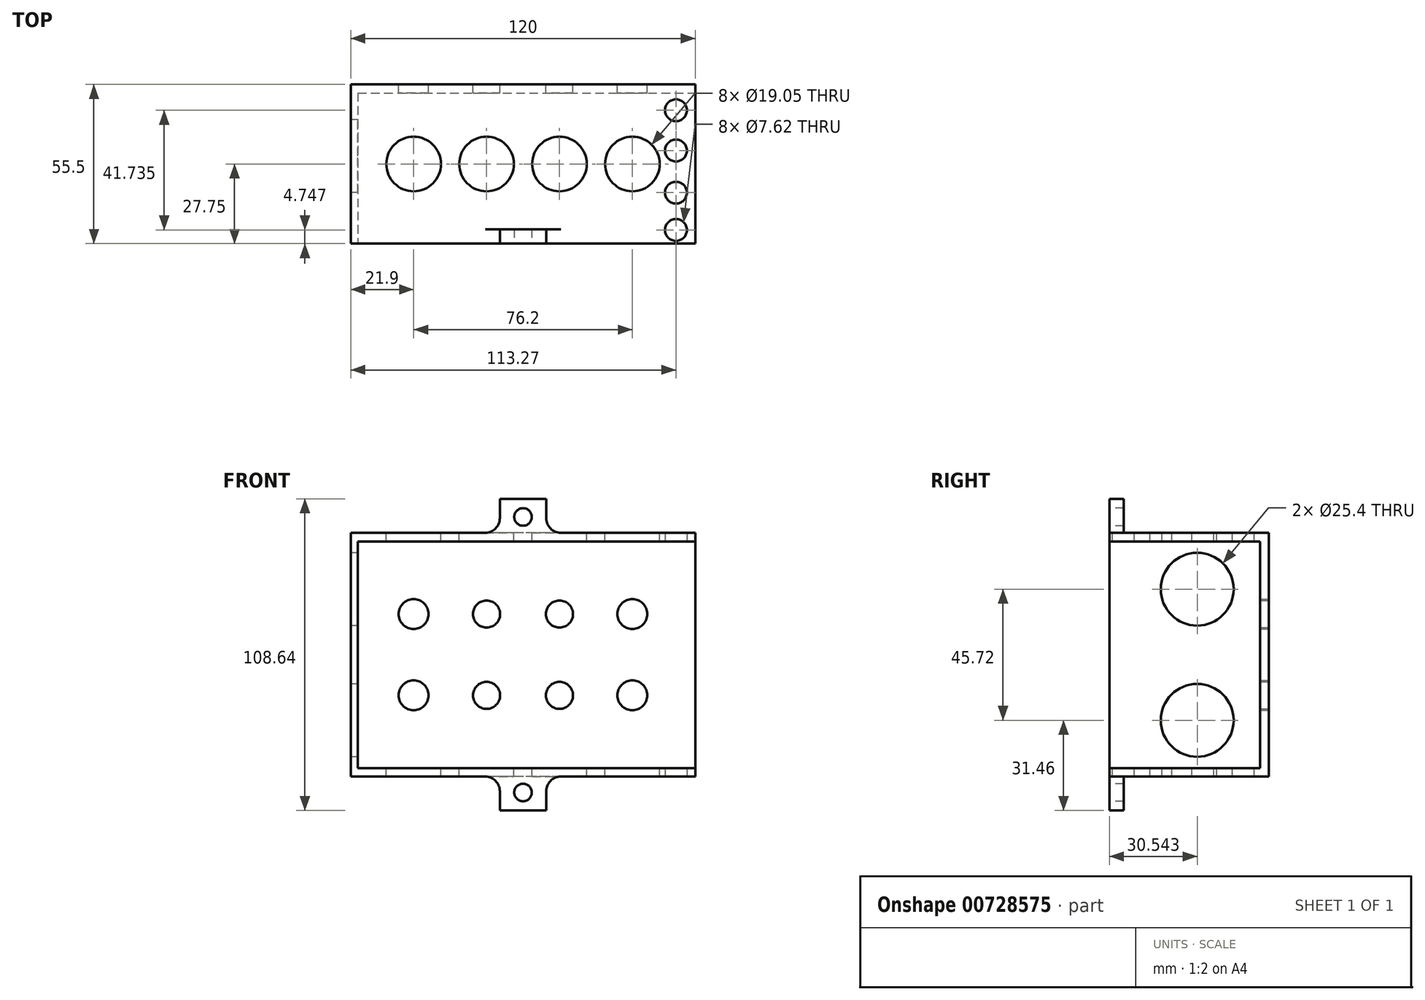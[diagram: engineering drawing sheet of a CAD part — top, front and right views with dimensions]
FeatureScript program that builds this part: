
annotation { "Feature Type Name" : "Feature", "Feature Type Description" : "" }
export const myFeature = defineFeature(function(context is Context, id is Id, definition is map)
    precondition{}
    {
        {
            var Q0;
            Q0=qCreatedBy(makeId("Front.planeOp"),FACE);
            var sketch = newSketch(context, id + "F0", { "sketchPlane" : qUnion([Q0])});
            skLineSegment(sketch, "E0.bottom", {"start": v(60, 42.5) * mm, "end": v(-60, 42.5) * mm});
            skLineSegment(sketch, "E0.top", {"start": v(60, -42.5) * mm, "end": v(-60, -42.5) * mm});
            skLineSegment(sketch, "E0.left", {"start": v(60, 42.5) * mm, "end": v(60, -42.5) * mm});
            skLineSegment(sketch, "E0.right", {"start": v(-60, 42.5) * mm, "end": v(-60, -42.5) * mm});
            skPoint(sketch, "E0.middle", {"position": v(0, 0) * mm});
            skCircle(sketch, "E1", {"center": v(-38.1, 14.17) * mm, "radius": 5.2 * mm});
            skCircle(sketch, "E2", {"center": v(-12.7, 14.17) * mm, "radius": 4.71 * mm});
            skCircle(sketch, "E3.MirrorC", {"center": v(12.7, 14.17) * mm, "radius": 4.71 * mm});
            skCircle(sketch, "E4.MirrorC", {"center": v(38.1, 14.17) * mm, "radius": 5.2 * mm});
            skCircle(sketch, "E5.MirrorC", {"center": v(-38.1, -14.17) * mm, "radius": 5.2 * mm});
            skCircle(sketch, "E6.MirrorC", {"center": v(-12.7, -14.17) * mm, "radius": 4.71 * mm});
            skCircle(sketch, "E7.MirrorC", {"center": v(12.7, -14.17) * mm, "radius": 4.71 * mm});
            skCircle(sketch, "E8.MirrorC", {"center": v(38.1, -14.17) * mm, "radius": 5.2 * mm});
            skSolve(sketch);
        }
        {
            var Q0;
            Q0 = qSketchRegion(id + "F0", true);
            extrude(context, id + "F1", {"entities" : qUnion([Q0]), "depth" : 3 * mm, "offsetDistance" : 25.4 * mm});
        }
        {
            var Q0;
            Q0=makeQuery(id+"F1.opExtrude","CAP_FACE",FACE,{"disambiguationData":[OSD([sQuery(id+"F0.wireOp",EDGE,"E0.bottom"),sQuery(id+"F0.wireOp",EDGE,"E0.top"),sQuery(id+"F0.wireOp",EDGE,"E0.left"),sQuery(id+"F0.wireOp",EDGE,"E0.right"),sQuery(id+"F0.wireOp",EDGE,"E1"),sQuery(id+"F0.wireOp",EDGE,"E2"),sQuery(id+"F0.wireOp",EDGE,"E3.MirrorC"),sQuery(id+"F0.wireOp",EDGE,"E4.MirrorC"),sQuery(id+"F0.wireOp",EDGE,"E5.MirrorC"),sQuery(id+"F0.wireOp",EDGE,"E6.MirrorC"),sQuery(id+"F0.wireOp",EDGE,"E7.MirrorC"),sQuery(id+"F0.wireOp",EDGE,"E8.MirrorC")])],"isStart":false});
            var sketch = newSketch(context, id + "F2", { "sketchPlane" : qUnion([Q0])});
            skLineSegment(sketch, "E9.bottom", {"start": v(-60, 42.5) * mm, "end": v(60, 42.5) * mm});
            skLineSegment(sketch, "E9.top", {"start": v(-60, 39.5) * mm, "end": v(60, 39.5) * mm});
            skLineSegment(sketch, "E9.left", {"start": v(-60, 42.5) * mm, "end": v(-60, 39.5) * mm});
            skLineSegment(sketch, "E9.right", {"start": v(60, 42.5) * mm, "end": v(60, 39.5) * mm});
            skLineSegment(sketch, "E10.MirrorCS", {"start": v(-60, -39.5) * mm, "end": v(60, -39.5) * mm});
            skLineSegment(sketch, "E11.MirrorCS", {"start": v(-60, -42.5) * mm, "end": v(60, -42.5) * mm});
            skSolve(sketch);
        }
        {
            var Q0;
            Q0 = qSketchRegion(id + "F2", true);
            extrude(context, id + "F3", {"entities" : qUnion([Q0]), "operationType" : NewBodyOperationType.ADD, "depth" : 52.5 * mm, "offsetDistance" : 25.4 * mm});
        }
        {
            var Q0;
            Q0=makeQuery(id+"F1.opExtrude","SWEPT_BODY",BODY,{"disambiguationData":[OSD([sQuery(id+"F0.wireOp",EDGE,"E0.bottom"),sQuery(id+"F0.wireOp",EDGE,"E0.top"),sQuery(id+"F0.wireOp",EDGE,"E0.left"),sQuery(id+"F0.wireOp",EDGE,"E0.right"),sQuery(id+"F0.wireOp",EDGE,"E1"),sQuery(id+"F0.wireOp",EDGE,"E2"),sQuery(id+"F0.wireOp",EDGE,"E3.MirrorC"),sQuery(id+"F0.wireOp",EDGE,"E4.MirrorC"),sQuery(id+"F0.wireOp",EDGE,"E5.MirrorC"),sQuery(id+"F0.wireOp",EDGE,"E6.MirrorC"),sQuery(id+"F0.wireOp",EDGE,"E7.MirrorC"),sQuery(id+"F0.wireOp",EDGE,"E8.MirrorC")])]});
            var Q1;
            Q1=qCreatedBy(makeId("Top.planeOp"),FACE);
            mirror(context, id + "F4", {"operationType" : NewBodyOperationType.ADD, "entities" : qUnion([Q0]), "mirrorPlane" : qUnion([Q1])});
        }
        {
            var Q0;
            Q0=makeQuery(id+"F3.opExtrude","CAP_FACE",FACE,{"disambiguationData":[OSD([sQuery(id+"F2.wireOp",EDGE,"E9.bottom"),sQuery(id+"F2.wireOp",EDGE,"E9.top"),sQuery(id+"F2.wireOp",EDGE,"E9.left"),sQuery(id+"F2.wireOp",EDGE,"E9.right")])],"isStart":false});
            var sketch = newSketch(context, id + "F5", { "sketchPlane" : qUnion([Q0])});
            skLineSegment(sketch, "E12.bottom", {"start": v(8.07, 54.32) * mm, "end": v(-8.07, 54.32) * mm});
            skLineSegment(sketch, "E12.top", {"start": v(8.07, 41.74) * mm, "end": v(-8.07, 41.74) * mm});
            skLineSegment(sketch, "E12.left", {"start": v(8.07, 54.32) * mm, "end": v(8.07, 41.74) * mm});
            skLineSegment(sketch, "E12.right", {"start": v(-8.07, 54.32) * mm, "end": v(-8.07, 41.74) * mm});
            skPoint(sketch, "E12.middle", {"position": v(0, 48.03) * mm});
            skCircle(sketch, "E13", {"center": v(0, 48.03) * mm, "radius": 3.06 * mm});
            skSolve(sketch);
        }
        {
            var Q0;
            Q0 = qSketchRegion(id + "F5", true);
            extrude(context, id + "F6", {"entities" : qUnion([Q0]), "operationType" : NewBodyOperationType.ADD, "oppositeDirection" : true, "depth" : 5 * mm, "offsetDistance" : 25.4 * mm});
        }
        {
            var Q0;
            Q0=makeQuery(id+"F6.boolean.opBoolean","INTERSECT",EDGE,{"derivedFrom":[makeQuery(id+"F3.boolean.opBoolean","MERGE",FACE,{"derivedFrom":[makeQuery(id+"F1.opExtrude","SWEPT_FACE",FACE,{"disambiguationData":[OSD([sQuery(id+"F0.wireOp",EDGE,"E0.bottom")])]}),makeQuery(id+"F3.opExtrude","SWEPT_FACE",FACE,{"disambiguationData":[OSD([sQuery(id+"F2.wireOp",EDGE,"E9.bottom")])]})]}),makeQuery(id+"F6.opExtrude","SWEPT_FACE",FACE,{"disambiguationData":[OSD([sQuery(id+"F5.wireOp",EDGE,"E12.right")])]})]});
            var Q1;
            Q1=makeQuery(id+"F6.boolean.opBoolean","INTERSECT",EDGE,{"derivedFrom":[makeQuery(id+"F3.boolean.opBoolean","MERGE",FACE,{"derivedFrom":[makeQuery(id+"F1.opExtrude","SWEPT_FACE",FACE,{"disambiguationData":[OSD([sQuery(id+"F0.wireOp",EDGE,"E0.bottom")])]}),makeQuery(id+"F3.opExtrude","SWEPT_FACE",FACE,{"disambiguationData":[OSD([sQuery(id+"F2.wireOp",EDGE,"E9.bottom")])]})]}),makeQuery(id+"F6.opExtrude","SWEPT_FACE",FACE,{"disambiguationData":[OSD([sQuery(id+"F5.wireOp",EDGE,"E12.left")])]})]});
            fillet(context, id + "F7", {"entities" : qUnion([Q0, Q1]), "radius" : 5.08 * mm, "tangentPropagation" : true, "allowEdgeOverflow" : false});
        }
        {
            var Q0;
            Q0=makeQuery(id+"F1.opExtrude","SWEPT_BODY",BODY,{"disambiguationData":[OSD([sQuery(id+"F0.wireOp",EDGE,"E0.bottom"),sQuery(id+"F0.wireOp",EDGE,"E0.top"),sQuery(id+"F0.wireOp",EDGE,"E0.left"),sQuery(id+"F0.wireOp",EDGE,"E0.right"),sQuery(id+"F0.wireOp",EDGE,"E1"),sQuery(id+"F0.wireOp",EDGE,"E2"),sQuery(id+"F0.wireOp",EDGE,"E3.MirrorC"),sQuery(id+"F0.wireOp",EDGE,"E4.MirrorC"),sQuery(id+"F0.wireOp",EDGE,"E5.MirrorC"),sQuery(id+"F0.wireOp",EDGE,"E6.MirrorC"),sQuery(id+"F0.wireOp",EDGE,"E7.MirrorC"),sQuery(id+"F0.wireOp",EDGE,"E8.MirrorC")])]});
            var Q1;
            Q1=qCreatedBy(makeId("Top.planeOp"),FACE);
            mirror(context, id + "F8", {"operationType" : NewBodyOperationType.ADD, "entities" : qUnion([Q0]), "mirrorPlane" : qUnion([Q1])});
        }
        {
            var Q0;
            Q0=makeQuery(id+"F3.boolean.opBoolean","MERGE",FACE,{"derivedFrom":[makeQuery(id+"F1.opExtrude","SWEPT_FACE",FACE,{"disambiguationData":[OSD([sQuery(id+"F0.wireOp",EDGE,"E0.bottom")])]}),makeQuery(id+"F3.opExtrude","SWEPT_FACE",FACE,{"disambiguationData":[OSD([sQuery(id+"F2.wireOp",EDGE,"E9.bottom")])]})]});
            var sketch = newSketch(context, id + "F9", { "sketchPlane" : qUnion([Q0])});
            skCircle(sketch, "E14", {"center": v(-38.1, -27.75) * mm, "radius": 9.53 * mm});
            skPoint(sketch, "E14.centerSnap0", {"position": v(-60, -27.75) * mm});
            skCircle(sketch, "E15", {"center": v(-12.7, -27.75) * mm, "radius": 9.53 * mm});
            skCircle(sketch, "E16.MirrorC", {"center": v(12.7, -27.75) * mm, "radius": 9.53 * mm});
            skCircle(sketch, "E17.MirrorC", {"center": v(38.1, -27.75) * mm, "radius": 9.53 * mm});
            skSolve(sketch);
        }
        {
            var Q0;
            Q0 = qSketchRegion(id + "F9", true);
            extrude(context, id + "F10", {"entities" : qUnion([Q0]), "operationType" : NewBodyOperationType.REMOVE, "oppositeDirection" : true, "depth" : 152.4 * mm, "offsetDistance" : 25.4 * mm});
        }
        {
            var Q0;
            Q0=makeQuery(id+"F1.opExtrude","CAP_FACE",FACE,{"disambiguationData":[OSD([sQuery(id+"F0.wireOp",EDGE,"E0.bottom"),sQuery(id+"F0.wireOp",EDGE,"E0.top"),sQuery(id+"F0.wireOp",EDGE,"E0.left"),sQuery(id+"F0.wireOp",EDGE,"E0.right"),sQuery(id+"F0.wireOp",EDGE,"E1"),sQuery(id+"F0.wireOp",EDGE,"E2"),sQuery(id+"F0.wireOp",EDGE,"E3.MirrorC"),sQuery(id+"F0.wireOp",EDGE,"E4.MirrorC"),sQuery(id+"F0.wireOp",EDGE,"E5.MirrorC"),sQuery(id+"F0.wireOp",EDGE,"E6.MirrorC"),sQuery(id+"F0.wireOp",EDGE,"E7.MirrorC"),sQuery(id+"F0.wireOp",EDGE,"E8.MirrorC")])],"isStart":false});
            var sketch = newSketch(context, id + "F11", { "sketchPlane" : qUnion([Q0])});
            skLineSegment(sketch, "E18.bottom", {"start": v(-60, -42.5) * mm, "end": v(-57.57, -42.5) * mm});
            skLineSegment(sketch, "E18.top", {"start": v(-60, 42.47) * mm, "end": v(-57.57, 42.47) * mm});
            skLineSegment(sketch, "E18.left", {"start": v(-60, -42.5) * mm, "end": v(-60, 42.47) * mm});
            skLineSegment(sketch, "E18.right", {"start": v(-57.57, -42.5) * mm, "end": v(-57.57, 42.47) * mm});
            skSolve(sketch);
        }
        {
            var Q0;
            Q0 = qSketchRegion(id + "F11", true);
            var Q1;
            Q1=makeQuery(id+"F6.boolean.opBoolean","MERGE",FACE,{"derivedFrom":[makeQuery(id+"F3.opExtrude","CAP_FACE",FACE,{"disambiguationData":[OSD([sQuery(id+"F2.wireOp",EDGE,"E9.bottom"),sQuery(id+"F2.wireOp",EDGE,"E9.top"),sQuery(id+"F2.wireOp",EDGE,"E9.left"),sQuery(id+"F2.wireOp",EDGE,"E9.right")])],"isStart":false}),makeQuery(id+"F6.opExtrude","CAP_FACE",FACE,{"disambiguationData":[OSD([sQuery(id+"F5.wireOp",EDGE,"E12.bottom"),sQuery(id+"F5.wireOp",EDGE,"E12.top"),sQuery(id+"F5.wireOp",EDGE,"E12.left"),sQuery(id+"F5.wireOp",EDGE,"E12.right"),sQuery(id+"F5.wireOp",EDGE,"E13")])],"isStart":true})]});
            extrude(context, id + "F12", {"entities" : qUnion([Q0]), "operationType" : NewBodyOperationType.ADD, "endBound" : BoundingType.UP_TO_SURFACE, "depth" : 50.8 * mm, "endBoundEntityFace" : qUnion([Q1]), "offsetDistance" : 25.4 * mm});
        }
        {
            var Q0;
            {var subQ0=makeQuery(id+"F3.boolean.opBoolean","MERGE",FACE,{"derivedFrom":[makeQuery(id+"F1.opExtrude","SWEPT_FACE",FACE,{"disambiguationData":[OSD([sQuery(id+"F0.wireOp",EDGE,"E0.right")])]}),makeQuery(id+"F3.opExtrude","SWEPT_FACE",FACE,{"disambiguationData":[OSD([sQuery(id+"F2.wireOp",EDGE,"E9.left")])]})]});Q0=makeQuery(id+"F12.boolean.opBoolean","MERGE",FACE,{"derivedFrom":[makeQuery(id+"F4.boolean.opBoolean","MERGE",FACE,{"derivedFrom":[subQ0,makeQuery(id+"F4.opPattern","COPY",FACE,{"derivedFrom":subQ0,"instanceName":"1"})]}),makeQuery(id+"F12.opExtrude","SWEPT_FACE",FACE,{"disambiguationData":[OSD([sQuery(id+"F11.wireOp",EDGE,"E18.left")])]})]});}
            var sketch = newSketch(context, id + "F13", { "sketchPlane" : qUnion([Q0])});
            skCircle(sketch, "E19", {"center": v(24.96, 22.86) * mm, "radius": 12.7 * mm});
            skCircle(sketch, "E20", {"center": v(24.96, -22.86) * mm, "radius": 12.7 * mm});
            skSolve(sketch);
        }
        {
            var Q0;
            Q0 = qSketchRegion(id + "F13", true);
            extrude(context, id + "F14", {"entities" : qUnion([Q0]), "operationType" : NewBodyOperationType.REMOVE, "oppositeDirection" : true, "depth" : 25.4 * mm, "offsetDistance" : 25.4 * mm});
        }
        {
            var Q0;
            Q0=makeQuery(id+"F4.boolean.opBoolean","MERGE",FACE,{"derivedFrom":[makeQuery(id+"F1.opExtrude","SWEPT_FACE",FACE,{"disambiguationData":[OSD([sQuery(id+"F0.wireOp",EDGE,"E0.top")])]}),makeQuery(id+"F4.opPattern","COPY",FACE,{"derivedFrom":makeQuery(id+"F3.boolean.opBoolean","MERGE",FACE,{"derivedFrom":[makeQuery(id+"F1.opExtrude","SWEPT_FACE",FACE,{"disambiguationData":[OSD([sQuery(id+"F0.wireOp",EDGE,"E0.bottom")])]}),makeQuery(id+"F3.opExtrude","SWEPT_FACE",FACE,{"disambiguationData":[OSD([sQuery(id+"F2.wireOp",EDGE,"E9.bottom")])]})]}),"instanceName":"1"})]});
            var sketch = newSketch(context, id + "F15", { "sketchPlane" : qUnion([Q0])});
            skCircle(sketch, "E21", {"center": v(53.27, 50.75) * mm, "radius": 3.81 * mm});
            skCircle(sketch, "E22", {"center": v(53.27, 37.75) * mm, "radius": 3.81 * mm});
            skCircle(sketch, "E23", {"center": v(53.27, 23.07) * mm, "radius": 3.81 * mm});
            skCircle(sketch, "E24", {"center": v(53.27, 9.02) * mm, "radius": 3.81 * mm});
            skSolve(sketch);
        }
        {
            var Q0;
            Q0 = qSketchRegion(id + "F15", true);
            extrude(context, id + "F16", {"entities" : qUnion([Q0]), "operationType" : NewBodyOperationType.REMOVE, "oppositeDirection" : true, "depth" : 152.4 * mm, "offsetDistance" : 25.4 * mm});
        }
    });
